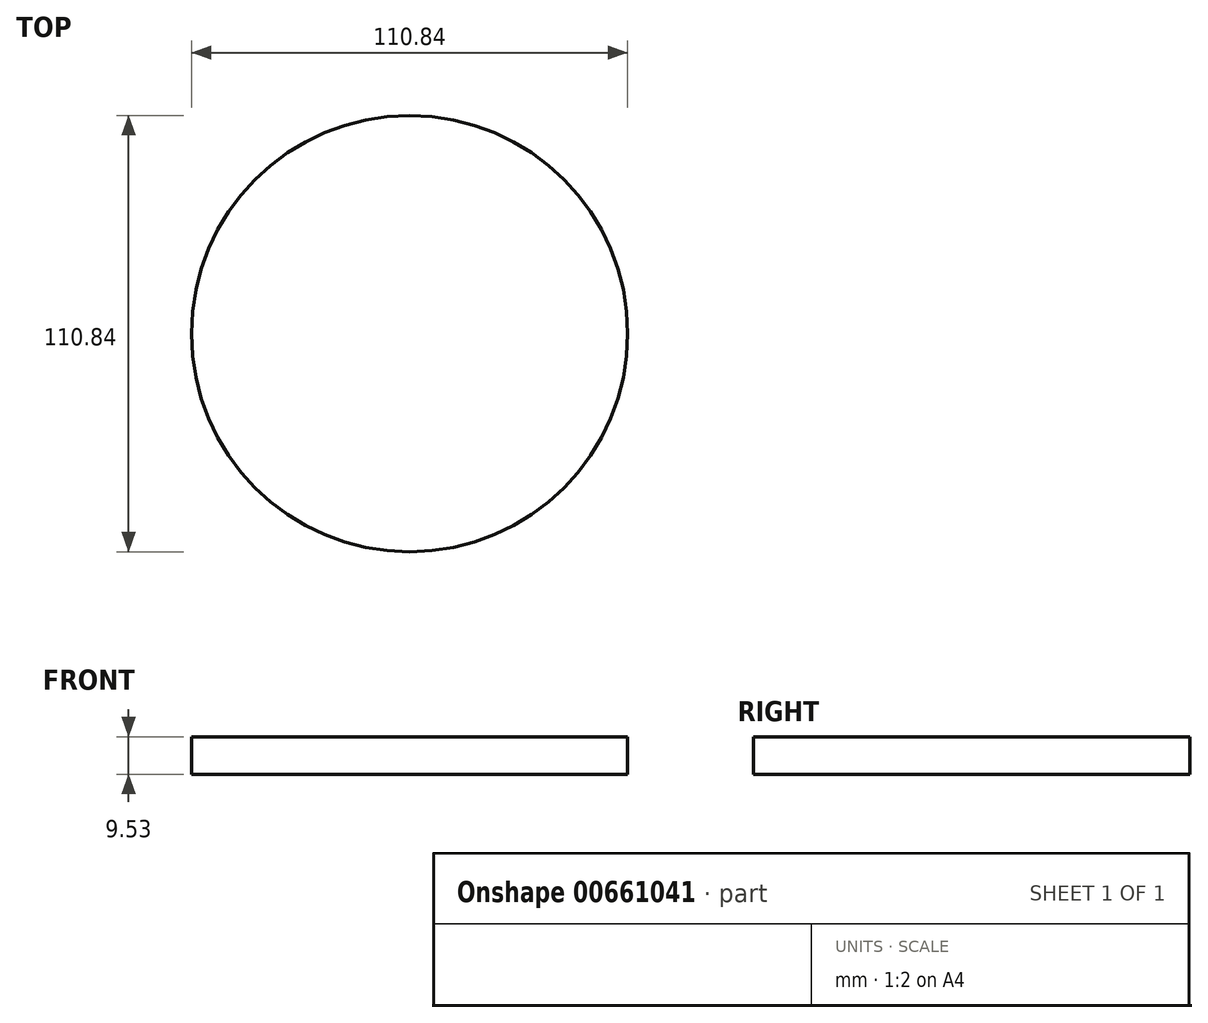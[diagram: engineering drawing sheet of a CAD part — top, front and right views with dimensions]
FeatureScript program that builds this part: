
annotation { "Feature Type Name" : "Feature", "Feature Type Description" : "" }
export const myFeature = defineFeature(function(context is Context, id is Id, definition is map)
    precondition{}
    {
        {
            var Q0;
            Q0=qCreatedBy(makeId("Top.planeOp"),FACE);
            var sketch = newSketch(context, id + "F0", { "sketchPlane" : qUnion([Q0])});
            skCircle(sketch, "E0", {"center": v(2.2, 0) * mm, "radius": 55.42 * mm});
            skSolve(sketch);
        }
        {
            var Q0;
            Q0=makeQuery(id+"F0.imprint","IMPRINT",FACE,{"disambiguationData":[TD([[makeQuery(id+"F0.imprint","IMPRINT",EDGE,{"derivedFrom":sQuery(id+"F0.wireOp",EDGE,"E0")}),1.0]])]});
            extrude(context, id + "F1", {"entities" : qUnion([Q0]), "oppositeDirection" : true, "depth" : 9.52 * mm, "offsetDistance" : 25.4 * mm});
        }
    });
